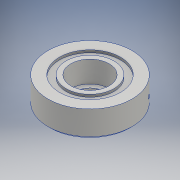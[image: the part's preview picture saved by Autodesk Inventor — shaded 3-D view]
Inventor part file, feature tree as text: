
AUTODESK INVENTOR PART (.ipt)
format: ipt  version: 2017 (Build 210142000, 142)  size: 197,120 bytes
history: native  units: mm
features: sketch x9, thread x8, hole x5, plane x4, extrude x3, chamfer x1, projected_geometry x1
ambient origin geometry x8: Origin, YZ Plane, XZ Plane, XY Plane, X Axis, Y Axis, Z Axis, Center Point
bodies: Solid1 (feature_tree)
feature tree (31):
  extrude  "Extrusion1"  Depth=24.0mm
  extrude  "Extrusion2"  Depth=51.0mm
  sketch  "Sketch3"  dims[d5=5.5mm d6=2.1mm d7=0.0mm]
  plane  "Work Plane1"
  plane  "Work Plane2"
  plane  "Work Plane3"
  plane  "Work Plane4"
  hole  "Hole1"  [1 undecoded]
  hole  "Hole2"  [1 undecoded]
  hole  "Hole3"  [1 undecoded]
  hole  "Hole4"  [1 undecoded]
  thread  "Thread1"  [1 undecoded]
  thread  "Thread2"  [1 undecoded]
  thread  "Thread3"  [1 undecoded]
  thread  "Thread4"  [1 undecoded]
  extrude  "Extrusion3"  Depth=10.0mm TaperAngle=0.0deg
  hole  "Hole6"  [1 undecoded]
  thread  "Thread9"  [1 undecoded]
  thread  "Thread10"  [1 undecoded]
  thread  "Thread11"  [1 undecoded]
  thread  "Thread12"  [1 undecoded]
  chamfer  "Chamfer2"  Distance=10.0mm
  sketch  "Sketch1"  dims[d0=70.0mm d1=24.0mm]
  sketch  "Sketch2"  dims[d2=22.0mm d3=0.0mm d4=51.0mm]
  projected_geometry  "Projected Loop1"
  sketch  "Sketch4"  dims[d11=6.684611mm d12=9.986774mm]
  sketch  "Sketch5"  dims[d13=13.0mm]
  sketch  "Sketch6"  dims[d14=3.0mm d15=6.0mm d16=4.0mm d17=2.0mm d18=90.0deg d19=4.0mm d20=20.594885mm d21=13.0mm]
  sketch  "Sketch7"  dims[d22=3.0mm d23=6.0mm d24=4.0mm d25=2.0mm d26=90.0deg d27=8.0mm d28=20.594885mm d29=13.0mm]
  sketch  "Sketch9"  dims[d30=3.0mm d31=6.0mm d32=4.0mm d33=2.0mm d34=90.0deg d35=8.0mm d36=20.594885mm d37=13.0mm]
  sketch  "Sketch11"  dims[d38=3.0mm d39=6.0mm d40=4.0mm d41=2.0mm d42=90.0deg d43=8.0mm d44=20.594885mm d45=10.0mm d46=0.0mm d47=10.0mm d48=0.0mm d49=10.0mm d50=0.0mm d51=10.0mm d52=0.0mm d53=32.0mm d54=18.0mm d55=0.0mm d77=54.0mm d78=40.0mm d80=360.0deg d82=3.0mm d83=6.0mm d84=4.0mm d85=2.0mm d86=90.0deg d87=8.0mm d88=20.594885mm d89=10.0mm d90=0.0mm d91=10.0mm d92=0.0mm d93=10.0mm d94=0.0mm d95=10.0mm d96=0.0mm d97=2.0mm d98=2.0mm d99=45.0deg]
note: 13 required parameter values undecoded (feature->parameter linkage not recoverable at this tier; creation-order binding heuristic only, values carry confidence <= 0.55)
